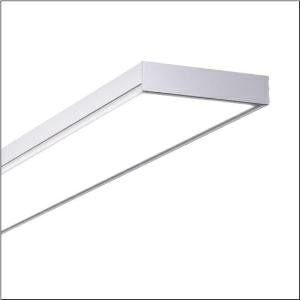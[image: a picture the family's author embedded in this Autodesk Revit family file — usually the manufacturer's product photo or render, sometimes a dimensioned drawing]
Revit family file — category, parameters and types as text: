
# Revit family: apollon_r__31_surface_51mp25wd2441ea_850e
name_source: partatom
category: Lighting Fixtures
units: mm (PartAtom-declared; Revit-internal decimal feet)

## family parameters
Cut with Voids When Loaded = No
Host = Face
Light Source = No
Part Type = Normal
Room Calculation Point = No
Round Connector Dimension = Use Diameter
Shared = No

## types (1)
- Apollon® 31 Surface (1 x LED, 3800 lm, 28 W, 4000K)
    Apparent Load = 28 VA
    CIE Flux Codes = 61 87 97 97 100
    Color Rendering = 80
    Color Temperature = 4000K
    Default Elevation = 1800 mm
    Description = Apollon® 31 Surface, office luminaire, primary optical cover: micro prismatic cover, of PMMA, light emission: direct distribution, primary light characteristic: symmetric, installation type: surface-mounted, LED, rated luminous flux: 3.800lm, luminous efficacy: 134lm/W, light colour: 840, colour temperature: 4000K, control gear: ECG DALI, with terminal, 5-pole, mains connection: 220..240V, AC, 50/60Hz, rated input power: 28W, housing, of sheet steel, coil coated, metallic grey (RAL 9006), length: 1.245mm, width: 200mm, height: 44mm, protection rating (complete): IP20, insulation class (complete): insulation class II (safety insulation), certification: CE, impact resistance: IK02, permissible operating ambient temperature: -20..+40°C, standard: EN 60598-2-22, packaging unit: 1 piece
    Height = 44 mm
    Lamp = 1 x LED
    Lamp Light Flux = 3800 lm
    Lamp Power = 28 W
    Lamp count = 1
    Length = 1245 mm
    Luminous efficacy = 136 lm/W
    Manufacturer = Siteco
    ModVariant = No
    Model = 51MP25WD2441EA
    Mounting Place = Ceiling
    Mounting Type = Surface mounted
    Number of Poles = 1
    OnlyDefault = Yes
    Power Factor = 1
    Product Name = Apollon® 31 Surface
    Product group = office luminaire | ceiling mounted
    ProductGroupID = 300
    Protection Class = Protection class II
    Protection Degree = IP 20
    RLX_Detail_Level = 1
    RLX_Emergency_Light_Flux = 0 lm
    RLX_Emergency_Type = 0
    RLX_Emergency_Type_DB = No
    RlxData = <blob elided: 24105 chars, md5=e765d65b>
    Socket = socket
    Standby Power = 0 W
    System Light Flux = 3800 lm
    System Power = 28 W
    Type Comments = Product without accessories
    Type Image = l_1313654.jpg
    URL = http://relux.com
    VarID = ---
    Voltage = 0 V
    Weight = 0.00 kg
    Width = 200 mm  [stored 0.656168 ft]

note: [stored X ft] marks values corroborated as IEEE doubles in the binary element streams (Revit-internal decimal feet)

## geometry (parser evidence)
native form markers: Blend x4, Sweep x10
no freeform markers — native parametric forms only
